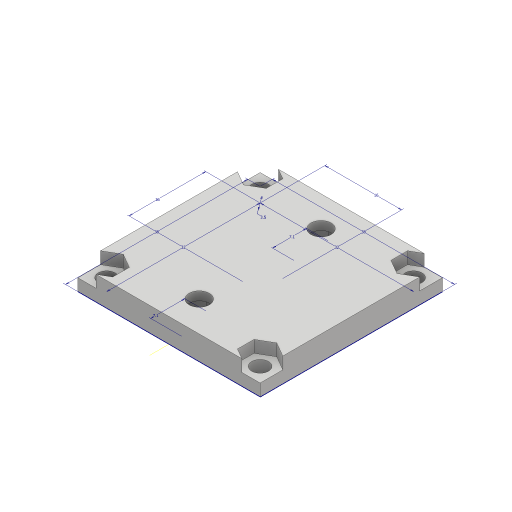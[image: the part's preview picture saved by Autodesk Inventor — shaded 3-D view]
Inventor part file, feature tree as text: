
AUTODESK INVENTOR PART (.ipt)
format: ipt  version: 2023 (Build 270158000, 158)  size: 185,344 bytes
history: native  units: mm
features: extrude x4, sketch x3, hole x1
ambient origin geometry x8: Origin, YZ Plane, XZ Plane, XY Plane, X Axis, Y Axis, Z Axis, Center Point
bodies: Body1 (feature_tree)
feature tree (8):
  sketch  "Sketch5"  dims[d47=3.5mm d48=20.0mm d50=32.0mm d51=20.0mm d53=32.0mm]
  extrude  "Extrusion3"  Depth=32.0mm
  extrude  "Extrusion4"  Depth=16.0mm
  extrude  "Extrusion5"  Depth=38.0mm
  hole  "Hole4"  [1 undecoded]
  extrude  "Extrusion6"  Depth=6.0mm
  sketch  "Sketch6"  dims[d56=16.0mm d57=16.0mm]
  sketch  "Sketch7"  dims[d58=38.0mm d59=38.0mm d60=5.0mm d61=0.0mm d62=6.0mm d63=20.0mm d65=32.0mm d66=20.0mm d68=32.0mm d71=2.5mm d72=0.0mm d73=7.1mm d74=7.1mm d75=3.2mm d76=0.0mm d77=4.2mm d78=6.0mm d79=4.0mm d80=2.0mm d81=90.0deg d82=8.0mm d83=20.594885mm d84=2.5mm d85=0.0mm]
note: 1 required parameter value undecoded (feature->parameter linkage not recoverable at this tier; creation-order binding heuristic only, values carry confidence <= 0.55)
